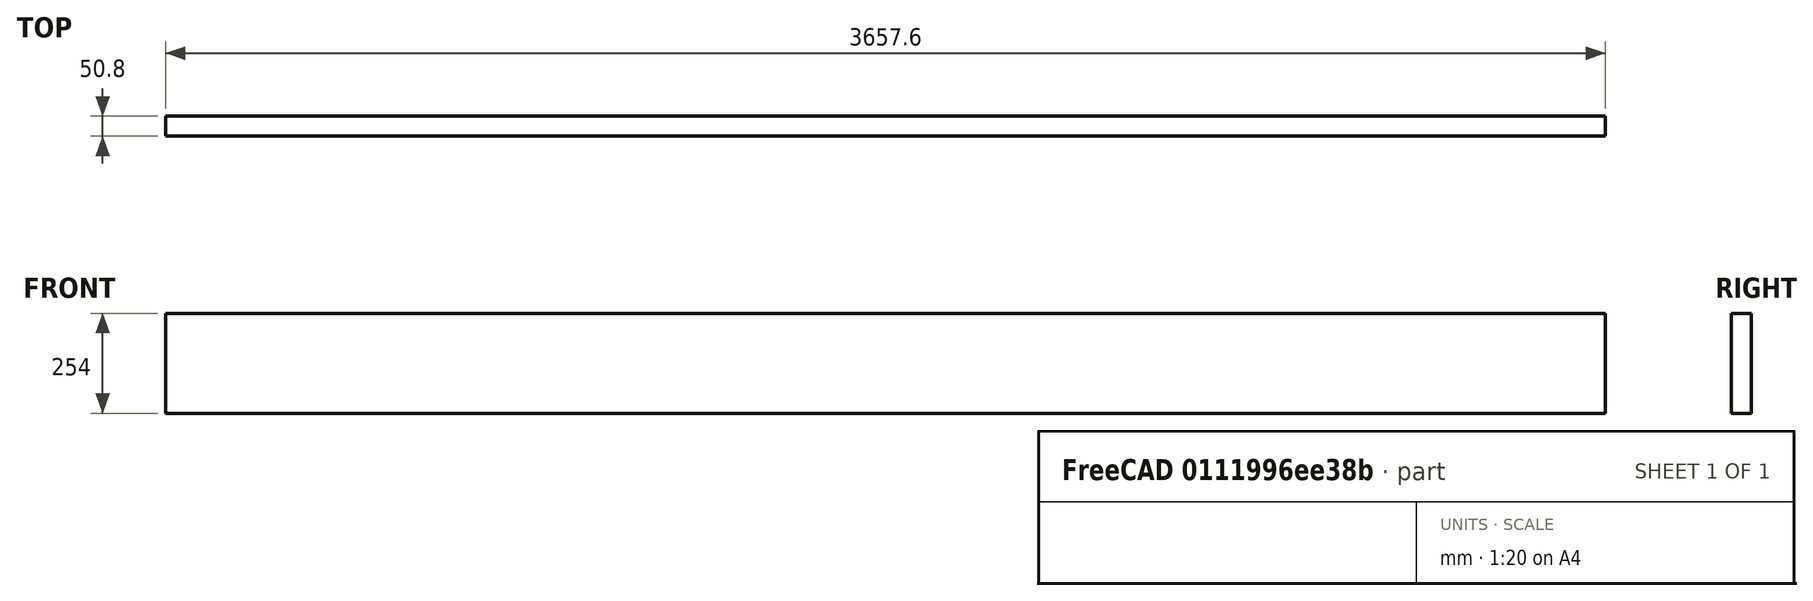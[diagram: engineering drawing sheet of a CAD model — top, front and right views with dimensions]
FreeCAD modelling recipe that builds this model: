
FCSTD DOCUMENT  (FreeCAD 0.20R29177 (Git))
Label: CrossMemberBack
License: All rights reserved
LicenseURL: http://en.wikipedia.org/wiki/All_rights_reserved
objects: Sketcher::SketchObject×1, PartDesign::Pad×1, PartDesign::Body×1
note: 4 computed .brp shape members not serialized (recipe doc carries the construction recipe); baked Part::Feature solids carry a one-line shape summary decoded from their .brp

FEATURE [Sketcher::SketchObject] Sketch
  FullyConstrained = true
  MapMode = 5
  Placement = pos=(0,0,0) rot=(0.57735,0.57735,0.57735;2.0944rad)
  Support = -> [YZ_Plane]
  sketch-geometry (4):
    g0: LineSegment StartX=0 StartY=0 StartZ=0 EndX=50.8 EndY=0 EndZ=0
    g1: LineSegment StartX=50.8 StartY=0 StartZ=0 EndX=50.8 EndY=254 EndZ=0
    g2: LineSegment StartX=50.8 StartY=254 StartZ=0 EndX=0 EndY=254 EndZ=0
    g3: LineSegment StartX=0 StartY=254 StartZ=0 EndX=0 EndY=0 EndZ=0
  constraints (11):
    c: Coincident(g0,g1)
    c: Coincident(g1,g2)
    c: Coincident(g2,g3)
    c: Coincident(g3,g0)
    c: Horizontal(g0)
    c: Horizontal(g2)
    c: Vertical(g1)
    c: Vertical(g3)
    c: Coincident(g0,g-1)
    c: DistanceX(g2,g2) = 50.8
    c: DistanceY(g3,g3) = 254
FEATURE [PartDesign::Pad] Pad
  Direction = (1,-2e-16,3e-16)
  Length = 3657.6
  Length2 = 9.525
  Placement = pos=(0,0,0) rot=(0.57735,0.57735,0.57735;2.0944rad)
  Profile = -> Sketch
  ReferenceAxis = -> Sketch [N_Axis]
  Type = 0
FEATURE [PartDesign::Body] Body
  Group = -> [Sketch,Pad]
  Origin = -> Origin
  Tip = -> Pad
